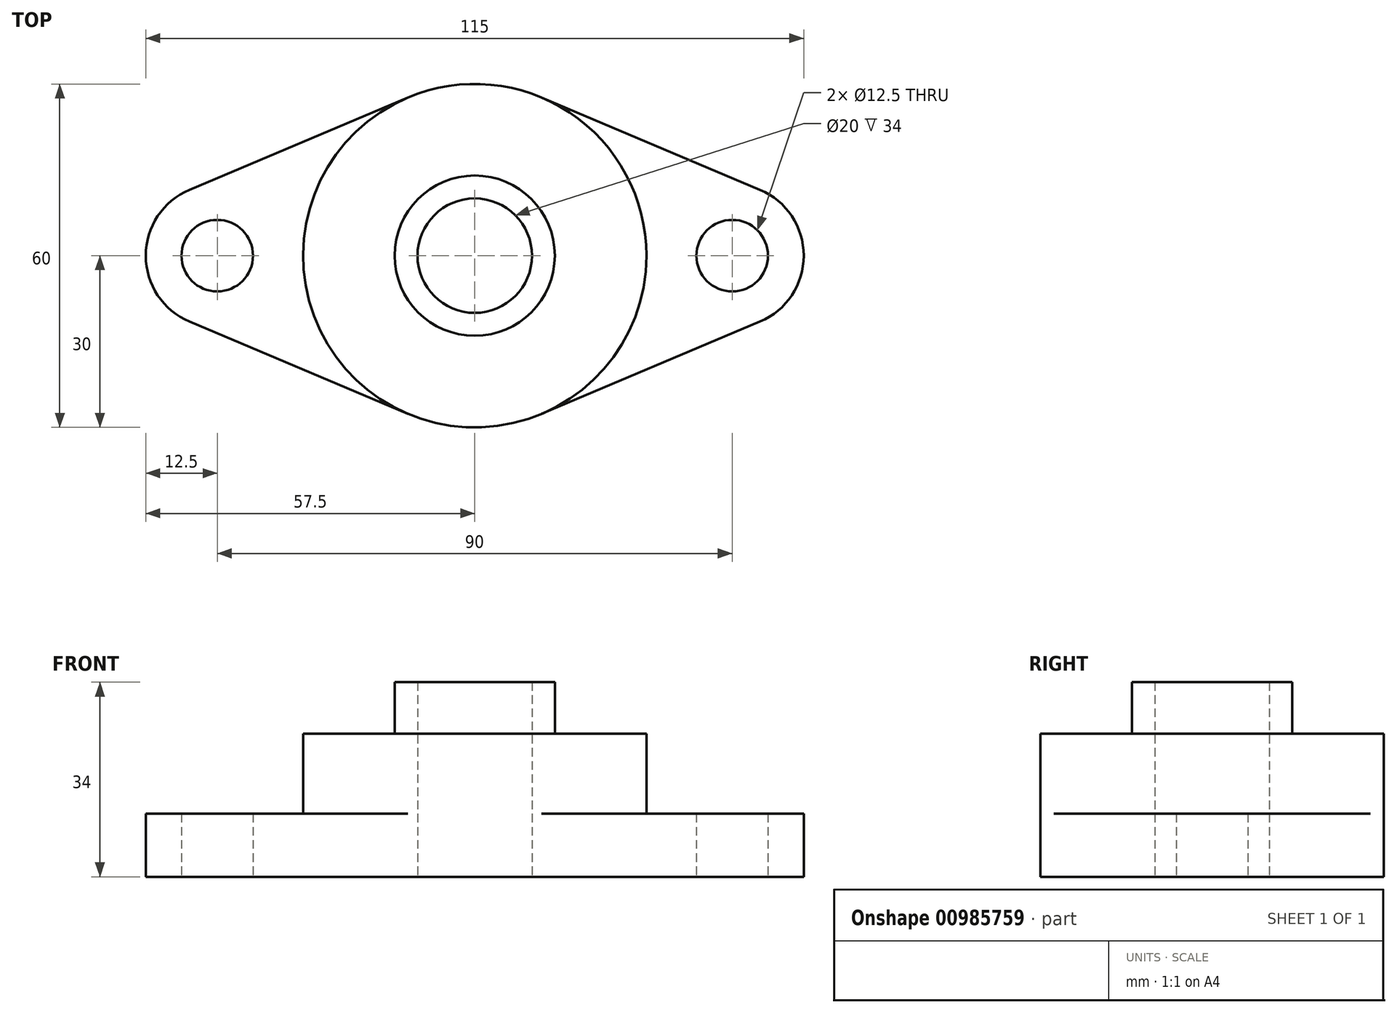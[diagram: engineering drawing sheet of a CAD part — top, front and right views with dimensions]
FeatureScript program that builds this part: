
annotation { "Feature Type Name" : "Feature", "Feature Type Description" : "" }
export const myFeature = defineFeature(function(context is Context, id is Id, definition is map)
    precondition{}
    {
        {
            var Q0;
            Q0=qCreatedBy(makeId("Top.planeOp"),FACE);
            var sketch = newSketch(context, id + "F0", { "sketchPlane" : qUnion([Q0])});
            skCircle(sketch, "E0", {"center": v(-45, 0) * mm, "radius": 6.25 * mm});
            skArc(sketch, "E1", {"start": v(-11.67, -27.64) * mm, "mid": v(0, -30) * mm, "end": v(11.67, -27.64) * mm});
            skArc(sketch, "E2", {"start": v(-49.86, 11.52) * mm, "mid": v(-57.5, 0) * mm, "end": v(-49.86, -11.52) * mm});
            skCircle(sketch, "E3.MirrorC", {"center": v(45, 0) * mm, "radius": 6.25 * mm});
            skArc(sketch, "E4.MirrorC", {"start": v(49.86, 11.52) * mm, "mid": v(57.5, 0) * mm, "end": v(49.86, -11.52) * mm});
            skLineSegment(sketch, "E5", {"start": v(-49.86, 11.52) * mm, "end": v(-11.67, 27.64) * mm});
            skLineSegment(sketch, "E6", {"start": v(11.67, 27.64) * mm, "end": v(49.86, 11.52) * mm});
            skLineSegment(sketch, "E7", {"start": v(11.67, -27.64) * mm, "end": v(49.86, -11.52) * mm});
            skLineSegment(sketch, "E8", {"start": v(-11.67, -27.64) * mm, "end": v(-49.86, -11.52) * mm});
            skArc(sketch, "E9.trimOffspring", {"start": v(11.67, 27.64) * mm, "mid": v(0, 30) * mm, "end": v(-11.67, 27.64) * mm});
            skSolve(sketch);
        }
        {
            var Q0;
            Q0=makeQuery(id+"F0.imprint","IMPRINT",FACE,{"disambiguationData":[TD([[makeQuery(id+"F0.imprint","IMPRINT",EDGE,{"derivedFrom":sQuery(id+"F0.wireOp",EDGE,"E0")}),-1.0]])]});
            extrude(context, id + "F1", {"entities" : qUnion([Q0]), "depth" : 11 * mm, "offsetDistance" : 25 * mm});
        }
        {
            var Q0;
            Q0=qCreatedBy(makeId("Top.planeOp"),FACE);
            var sketch = newSketch(context, id + "F2", { "sketchPlane" : qUnion([Q0])});
            skCircle(sketch, "E10", {"center": v(0, 0) * mm, "radius": 30 * mm});
            skSolve(sketch);
        }
        {
            var Q0;
            Q0=makeQuery(id+"F2.imprint","IMPRINT",FACE,{"disambiguationData":[TD([[makeQuery(id+"F2.imprint","IMPRINT",EDGE,{"derivedFrom":sQuery(id+"F2.wireOp",EDGE,"E10")}),1.0]])]});
            extrude(context, id + "F3", {"entities" : qUnion([Q0]), "operationType" : NewBodyOperationType.ADD, "depth" : 25 * mm, "offsetDistance" : 25 * mm});
        }
        {
            var Q0;
            Q0=qCreatedBy(makeId("Top.planeOp"),FACE);
            var sketch = newSketch(context, id + "F4", { "sketchPlane" : qUnion([Q0])});
            skCircle(sketch, "E11", {"center": v(0, 0) * mm, "radius": 14 * mm});
            skCircle(sketch, "E12", {"center": v(0, 0) * mm, "radius": 10 * mm});
            skSolve(sketch);
        }
        {
            var Q0;
            Q0=makeQuery(id+"F4.imprint","IMPRINT",FACE,{"disambiguationData":[TD([[makeQuery(id+"F4.imprint","IMPRINT",EDGE,{"derivedFrom":sQuery(id+"F4.wireOp",EDGE,"E11")}),1.0]])]});
            extrude(context, id + "F5", {"entities" : qUnion([Q0]), "operationType" : NewBodyOperationType.ADD, "depth" : 34 * mm, "offsetDistance" : 25 * mm});
        }
        {
            var Q0;
            Q0=makeQuery(id+"F5.boolean.opBoolean","SPLIT",FACE,{"disambiguationData":[TD([makeQuery(id+"F5.opExtrude","SWEPT_FACE",FACE,{"disambiguationData":[OSD([sQuery(id+"F4.wireOp",EDGE,"E12")])]})])],"derivedFrom":makeQuery(id+"F3.opExtrude","CAP_FACE",FACE,{"disambiguationData":[OSD([sQuery(id+"F2.wireOp",EDGE,"E10")])],"isStart":false})});
            extrude(context, id + "F6", {"entities" : qUnion([Q0]), "operationType" : NewBodyOperationType.REMOVE, "oppositeDirection" : true, "depth" : 25 * mm, "offsetDistance" : 25 * mm});
        }
    });
